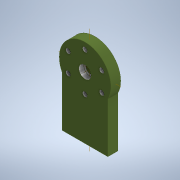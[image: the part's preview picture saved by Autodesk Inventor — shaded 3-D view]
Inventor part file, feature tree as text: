
AUTODESK INVENTOR PART (.ipt)
format: ipt  version: 2021.1 (Build 251245000, 245)  size: 265,728 bytes
history: native  units: in
note: dims shown in document units (in); Inventor stores cm internally (conversion verified against a paired STEP export)
features: extrude x6, sketch x4, chamfer x2, fillet x1
ambient origin geometry x8: Origin, YZ Plane, XZ Plane, XY Plane, X Axis, Y Axis, Z Axis, Center Point
bodies: Solid1 (feature_tree)
feature tree (13):
  sketch  "Sketch1"  dims[d0=10.4in d1=7.8in]
  extrude  "Extrusion1"  Depth=7.8in
  sketch  "Sketch2"  dims[d8=0.7in d9=2.3622in d11=360.0deg]
  extrude  "Extrusion2"  Depth=2.3622in TaperAngle=360.0deg
  extrude  "Extrusion3"  Depth=1.0in TaperAngle=0.0deg
  extrude  "Extrusion4"  Depth=9.2in
  fillet  "Fillet1"  Radius=4.6in
  chamfer  "Chamfer1"  Distance=12.5in
  chamfer  "Chamfer2"  Distance=1.2225in
  extrude  "Extrusion5"  Depth=2.0in TaperAngle=0.0deg
  extrude  "Extrusion6"  Depth=2.5in
  sketch  "Sketch3"  dims[d13=1.6in d14=1.0in d15=0.0in]
  sketch  "Sketch5"  dims[d16=5.2in d17=9.2in d18=4.6in d19=12.5in d20=1.2225in d21=2.0in d22=0.0in d23=2.5in d24=1.2in d25=1.2in d26=1.2in d27=0.6in d28=0.4in d29=0.0in d30=0.3956in d31=1.0in d32=0.0in d33=0.2in d34=0.01in d35=0.125in d36=45.0deg d37=0.01in d38=0.125in d39=45.0deg d40=1.0in d41=2.3622in d43=360.0deg d45=1.0in d46=2.3622in d48=360.0deg d50=0.6in d51=0.0in d55=3.0in d56=3.0in d57=1.0in d58=1.0in d59=2.0in d60=0.0in]
